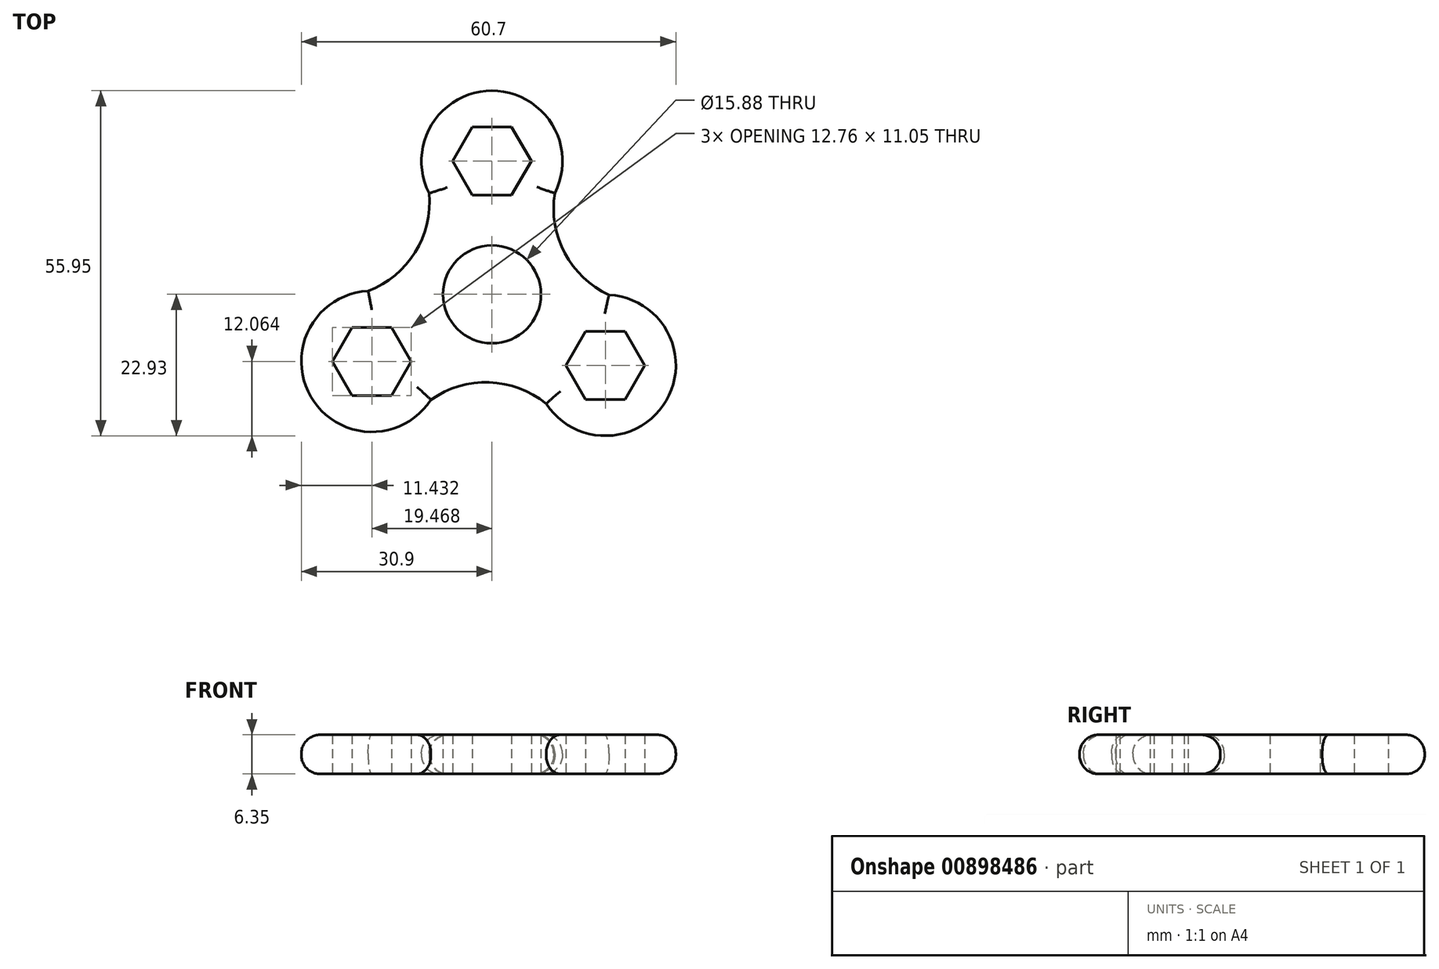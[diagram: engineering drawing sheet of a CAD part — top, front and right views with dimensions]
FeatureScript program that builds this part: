
annotation { "Feature Type Name" : "Feature", "Feature Type Description" : "" }
export const myFeature = defineFeature(function(context is Context, id is Id, definition is map)
    precondition{}
    {
        {
            var Q0;
            Q0=qCreatedBy(makeId("Top.planeOp"),FACE);
            var sketch = newSketch(context, id + "F0", { "sketchPlane" : qUnion([Q0])});
            skArc(sketch, "E0", {"start": v(10.19, 16.4) * mm, "mid": v(0, 33.02) * mm, "end": v(-10.19, 16.4) * mm});
            skCircle(sketch, "E1", {"center": v(0, 0) * mm, "radius": 7.94 * mm});
            skCircle(sketch, "E2.cCircle", {"center": v(0, 21.59) * mm, "radius": 5.52 * mm, "construction": true});
            skLineSegment(sketch, "E2.0", {"start": v(-3.19, 27.11) * mm, "end": v(3.19, 27.11) * mm});
            skLineSegment(sketch, "E2.1", {"start": v(3.19, 27.11) * mm, "end": v(6.38, 21.59) * mm});
            skLineSegment(sketch, "E2.2", {"start": v(6.38, 21.59) * mm, "end": v(3.19, 16.07) * mm});
            skLineSegment(sketch, "E2.3", {"start": v(3.19, 16.07) * mm, "end": v(-3.19, 16.07) * mm});
            skLineSegment(sketch, "E2.4", {"start": v(-3.19, 16.07) * mm, "end": v(-6.38, 21.59) * mm});
            skLineSegment(sketch, "E2.5", {"start": v(-6.38, 21.59) * mm, "end": v(-3.19, 27.11) * mm});
            skPoint(sketch, "E2.0.midPoint", {"position": v(0, 27.11) * mm});
            skArc(sketch, "E3.1.0", {"start": v(-20.07, 0.55) * mm, "mid": v(-29.37, -16.58) * mm, "end": v(-9.89, -17.1) * mm});
            skArc(sketch, "E3.2.0", {"start": v(8.8, -17.73) * mm, "mid": v(28.27, -17.21) * mm, "end": v(18.98, -0.08) * mm});
            skPoint(sketch, "E3.center", {"position": v(-0.36, -0.26) * mm});
            skLineSegment(sketch, "E4.1.0", {"start": v(-22.66, -5.34) * mm, "end": v(-16.28, -5.34) * mm});
            skLineSegment(sketch, "E4.1.1", {"start": v(-25.85, -10.87) * mm, "end": v(-22.66, -5.34) * mm});
            skLineSegment(sketch, "E4.1.2", {"start": v(-22.66, -16.4) * mm, "end": v(-25.85, -10.87) * mm});
            skLineSegment(sketch, "E4.1.3", {"start": v(-16.28, -16.4) * mm, "end": v(-22.66, -16.4) * mm});
            skLineSegment(sketch, "E4.1.4", {"start": v(-13.09, -10.87) * mm, "end": v(-16.28, -16.4) * mm});
            skLineSegment(sketch, "E4.1.5", {"start": v(-16.28, -5.34) * mm, "end": v(-13.09, -10.87) * mm});
            skLineSegment(sketch, "E4.2.0", {"start": v(15.18, -17.02) * mm, "end": v(12, -11.5) * mm});
            skLineSegment(sketch, "E4.2.1", {"start": v(21.56, -17.02) * mm, "end": v(15.18, -17.02) * mm});
            skLineSegment(sketch, "E4.2.2", {"start": v(24.75, -11.5) * mm, "end": v(21.56, -17.02) * mm});
            skLineSegment(sketch, "E4.2.3", {"start": v(21.56, -5.97) * mm, "end": v(24.75, -11.5) * mm});
            skLineSegment(sketch, "E4.2.4", {"start": v(15.18, -5.97) * mm, "end": v(21.56, -5.97) * mm});
            skLineSegment(sketch, "E4.2.5", {"start": v(12, -11.5) * mm, "end": v(15.18, -5.97) * mm});
            skArc(sketch, "E5.MirrorCS", {"start": v(18.98, -0.08) * mm, "mid": v(11.8, 6.68) * mm, "end": v(10.19, 16.4) * mm});
            skArc(sketch, "E6.1.0", {"start": v(-10.19, 16.4) * mm, "mid": v(-12.46, 6.81) * mm, "end": v(-20.07, 0.55) * mm});
            skArc(sketch, "E6.2.0", {"start": v(-9.89, -17.1) * mm, "mid": v(-0.44, -14.27) * mm, "end": v(8.8, -17.73) * mm});
            skSolve(sketch);
        }
        {
            var Q0;
            Q0=makeQuery(id+"F0.imprint","IMPRINT",FACE,{"disambiguationData":[TD([[makeQuery(id+"F0.imprint","IMPRINT",EDGE,{"derivedFrom":sQuery(id+"F0.wireOp",EDGE,"XCEXlE6d-D8l5-pcnz-RzQe-CXv54Aw19pjo")}),1.0]])]});
            var Q1;
            Q1=makeQuery(id+"F0.imprint","IMPRINT",FACE,{"disambiguationData":[TD([[makeQuery(id+"F0.imprint","IMPRINT",EDGE,{"derivedFrom":sQuery(id+"F0.wireOp",EDGE,"E0")}),1.0]])]});
            extrude(context, id + "F1", {"entities" : qUnion([Q0, Q1]), "depth" : 6.35 * mm, "offsetDistance" : 25.4 * mm});
        }
        {
            var Q0;
            Q0=makeQuery(id+"F1.opExtrude","CAP_EDGE",EDGE,{"disambiguationData":[OSD([sQuery(id+"F0.wireOp",EDGE,"E3.1.0")])],"isStart":false});
            var Q1;
            Q1=makeQuery(id+"F1.opExtrude","CAP_EDGE",EDGE,{"disambiguationData":[OSD([sQuery(id+"F0.wireOp",EDGE,"E3.1.0")])],"isStart":true});
            var Q2;
            Q2=makeQuery(id+"F1.opExtrude","CAP_EDGE",EDGE,{"disambiguationData":[OSD([sQuery(id+"F0.wireOp",EDGE,"E6.2.0")])],"isStart":false});
            var Q3;
            Q3=makeQuery(id+"F1.opExtrude","CAP_EDGE",EDGE,{"disambiguationData":[OSD([sQuery(id+"F0.wireOp",EDGE,"E6.2.0")])],"isStart":true});
            var Q4;
            Q4=makeQuery(id+"F1.opExtrude","CAP_EDGE",EDGE,{"disambiguationData":[OSD([sQuery(id+"F0.wireOp",EDGE,"E3.2.0")])],"isStart":false});
            var Q5;
            Q5=makeQuery(id+"F1.opExtrude","CAP_EDGE",EDGE,{"disambiguationData":[OSD([sQuery(id+"F0.wireOp",EDGE,"E3.2.0")])],"isStart":true});
            var Q6;
            Q6=makeQuery(id+"F1.opExtrude","CAP_EDGE",EDGE,{"disambiguationData":[OSD([sQuery(id+"F0.wireOp",EDGE,"E5.MirrorCS")])],"isStart":true});
            var Q7;
            Q7=makeQuery(id+"F1.opExtrude","CAP_EDGE",EDGE,{"disambiguationData":[OSD([sQuery(id+"F0.wireOp",EDGE,"E5.MirrorCS")])],"isStart":false});
            var Q8;
            Q8=makeQuery(id+"F1.opExtrude","CAP_EDGE",EDGE,{"disambiguationData":[OSD([sQuery(id+"F0.wireOp",EDGE,"E0")])],"isStart":false});
            var Q9;
            Q9=makeQuery(id+"F1.opExtrude","CAP_EDGE",EDGE,{"disambiguationData":[OSD([sQuery(id+"F0.wireOp",EDGE,"E0")])],"isStart":true});
            var Q10;
            Q10=makeQuery(id+"F1.opExtrude","CAP_EDGE",EDGE,{"disambiguationData":[OSD([sQuery(id+"F0.wireOp",EDGE,"E6.1.0")])],"isStart":false});
            var Q11;
            Q11=makeQuery(id+"F1.opExtrude","CAP_EDGE",EDGE,{"disambiguationData":[OSD([sQuery(id+"F0.wireOp",EDGE,"E6.1.0")])],"isStart":true});
            fillet(context, id + "F2", {"entities" : qUnion([Q0, Q1, Q2, Q3, Q4, Q5, Q6, Q7, Q8, Q9, Q10, Q11]), "radius" : 3.05 * mm, "tangentPropagation" : true, "allowEdgeOverflow" : false});
        }
    });
